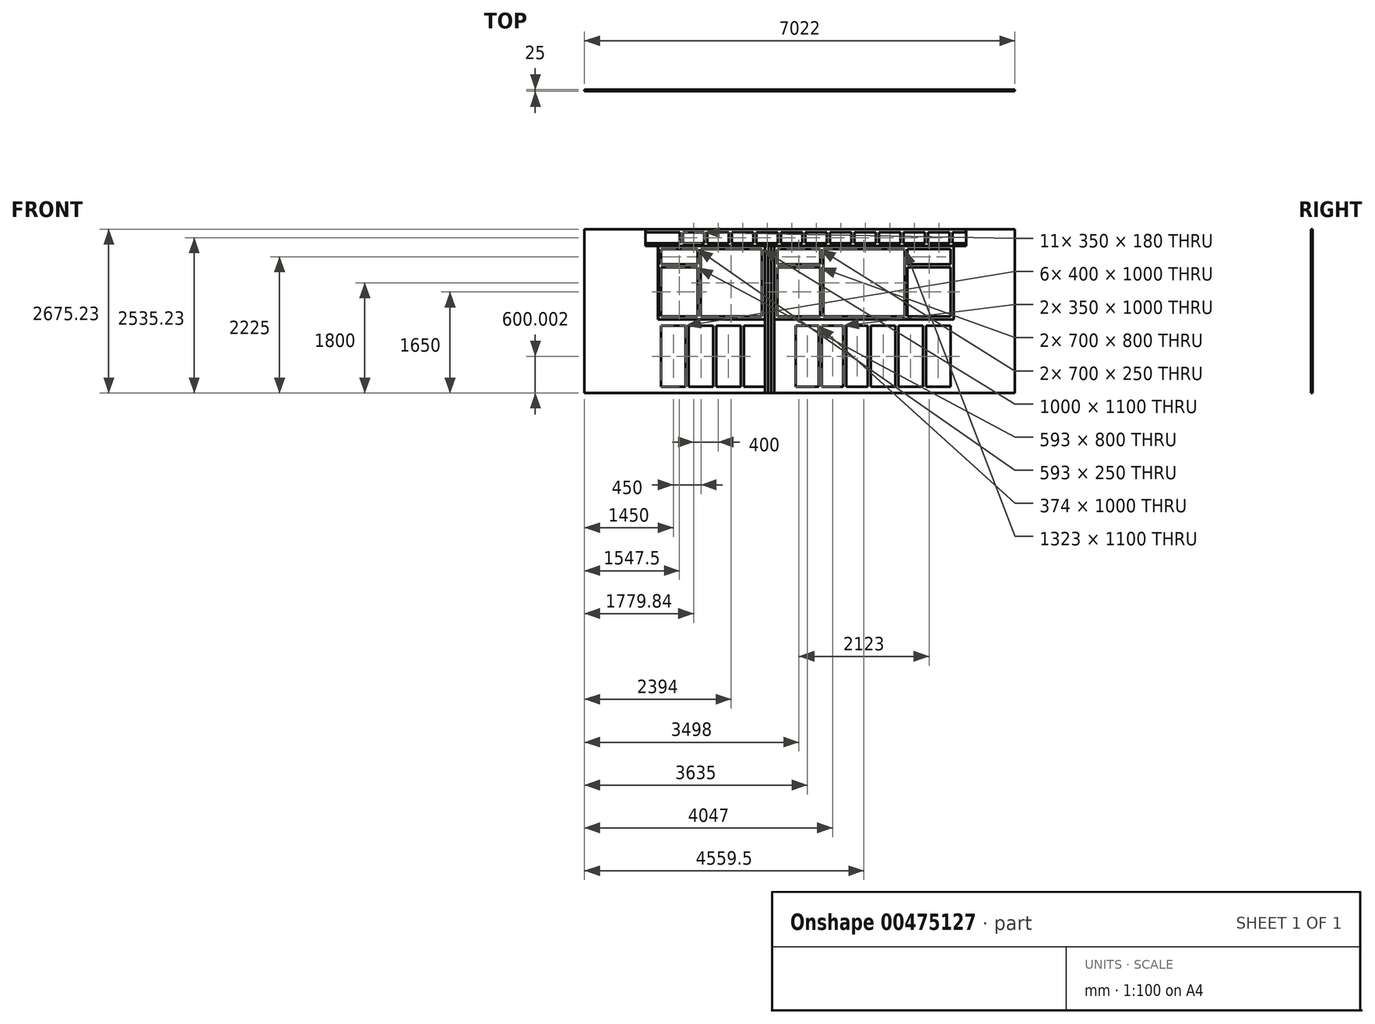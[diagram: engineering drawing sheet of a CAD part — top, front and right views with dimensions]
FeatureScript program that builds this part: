
annotation { "Feature Type Name" : "Feature", "Feature Type Description" : "" }
export const myFeature = defineFeature(function(context is Context, id is Id, definition is map)
    precondition{}
    {
        {
            var Q0;
            Q0=qCreatedBy(makeId("Front.planeOp"),FACE);
            var sketch = newSketch(context, id + "F0", { "sketchPlane" : qUnion([Q0])});
            skLineSegment(sketch, "E0.bottom", {"start": v(-708.07, 267.82) * mm, "end": v(4511.93, 267.82) * mm});
            skLineSegment(sketch, "E0.top", {"start": v(-708.07, 217.82) * mm, "end": v(4511.93, 217.82) * mm});
            skLineSegment(sketch, "E0.left", {"start": v(-708.07, 267.82) * mm, "end": v(-708.07, 217.82) * mm});
            skLineSegment(sketch, "E0.right", {"start": v(4511.93, 267.82) * mm, "end": v(4511.93, 217.82) * mm});
            skPoint(sketch, "E1.firstSnap0", {"position": v(-708.07, 242.82) * mm});
            skLineSegment(sketch, "E1.bottom", {"start": v(-708.07, 37.82) * mm, "end": v(4511.93, 37.82) * mm});
            skLineSegment(sketch, "E1.top", {"start": v(-708.07, -6.4) * mm, "end": v(4511.93, -6.4) * mm});
            skLineSegment(sketch, "E1.left", {"start": v(-708.07, 37.82) * mm, "end": v(-708.07, -6.4) * mm});
            skLineSegment(sketch, "E1.right", {"start": v(4511.93, 37.82) * mm, "end": v(4511.93, -6.4) * mm});
            skLineSegment(sketch, "E2.bottom", {"start": v(-554.23, 217.82) * mm, "end": v(-504.23, 217.82) * mm});
            skLineSegment(sketch, "E2.top", {"start": v(-554.23, 37.82) * mm, "end": v(-504.23, 37.82) * mm});
            skLineSegment(sketch, "E2.left", {"start": v(-554.23, 217.82) * mm, "end": v(-554.23, 37.82) * mm});
            skLineSegment(sketch, "E2.right", {"start": v(-504.23, 217.82) * mm, "end": v(-504.23, 37.82) * mm});
            skLineSegment(sketch, "E3.1.0.0", {"start": v(-154.23, 217.82) * mm, "end": v(-154.23, 37.82) * mm});
            skLineSegment(sketch, "E3.1.0.1", {"start": v(-104.23, 217.82) * mm, "end": v(-104.23, 37.82) * mm});
            skLineSegment(sketch, "E3.1.0.2", {"start": v(-154.23, 217.82) * mm, "end": v(-104.23, 217.82) * mm});
            skLineSegment(sketch, "E3.2.0.0", {"start": v(245.77, 217.82) * mm, "end": v(245.77, 37.82) * mm});
            skLineSegment(sketch, "E3.2.0.1", {"start": v(295.77, 217.82) * mm, "end": v(295.77, 37.82) * mm});
            skLineSegment(sketch, "E3.2.0.2", {"start": v(245.77, 217.82) * mm, "end": v(295.77, 217.82) * mm});
            skLineSegment(sketch, "E3.3.0.0", {"start": v(645.77, 217.82) * mm, "end": v(645.77, 37.82) * mm});
            skLineSegment(sketch, "E3.3.0.1", {"start": v(695.77, 217.82) * mm, "end": v(695.77, 37.82) * mm});
            skLineSegment(sketch, "E3.3.0.2", {"start": v(645.77, 217.82) * mm, "end": v(695.77, 217.82) * mm});
            skLineSegment(sketch, "E3.4.0.0", {"start": v(1045.77, 217.82) * mm, "end": v(1045.77, 37.82) * mm});
            skLineSegment(sketch, "E3.4.0.1", {"start": v(1095.77, 217.82) * mm, "end": v(1095.77, 37.82) * mm});
            skLineSegment(sketch, "E3.4.0.2", {"start": v(1045.77, 217.82) * mm, "end": v(1095.77, 217.82) * mm});
            skLineSegment(sketch, "E3.5.0.0", {"start": v(1445.77, 217.82) * mm, "end": v(1445.77, 37.82) * mm});
            skLineSegment(sketch, "E3.5.0.1", {"start": v(1495.77, 217.82) * mm, "end": v(1495.77, 37.82) * mm});
            skLineSegment(sketch, "E3.5.0.2", {"start": v(1445.77, 217.82) * mm, "end": v(1495.77, 217.82) * mm});
            skLineSegment(sketch, "E3.6.0.0", {"start": v(1845.77, 217.82) * mm, "end": v(1845.77, 37.82) * mm});
            skLineSegment(sketch, "E3.6.0.1", {"start": v(1895.77, 217.82) * mm, "end": v(1895.77, 37.82) * mm});
            skLineSegment(sketch, "E3.6.0.2", {"start": v(1845.77, 217.82) * mm, "end": v(1895.77, 217.82) * mm});
            skLineSegment(sketch, "E3.7.0.0", {"start": v(2245.77, 217.82) * mm, "end": v(2245.77, 37.82) * mm});
            skLineSegment(sketch, "E3.7.0.1", {"start": v(2295.77, 217.82) * mm, "end": v(2295.77, 37.82) * mm});
            skLineSegment(sketch, "E3.7.0.2", {"start": v(2245.77, 217.82) * mm, "end": v(2295.77, 217.82) * mm});
            skLineSegment(sketch, "E3.8.0.0", {"start": v(2645.77, 217.82) * mm, "end": v(2645.77, 37.82) * mm});
            skLineSegment(sketch, "E3.8.0.1", {"start": v(2695.77, 217.82) * mm, "end": v(2695.77, 37.82) * mm});
            skLineSegment(sketch, "E3.8.0.2", {"start": v(2645.77, 217.82) * mm, "end": v(2695.77, 217.82) * mm});
            skLineSegment(sketch, "E3.9.0.0", {"start": v(3045.77, 217.82) * mm, "end": v(3045.77, 37.82) * mm});
            skLineSegment(sketch, "E3.9.0.1", {"start": v(3095.77, 217.82) * mm, "end": v(3095.77, 37.82) * mm});
            skLineSegment(sketch, "E3.9.0.2", {"start": v(3045.77, 217.82) * mm, "end": v(3095.77, 217.82) * mm});
            skLineSegment(sketch, "E3.direction1", {"start": v(-554.23, 37.82) * mm, "end": v(-154.23, 37.82) * mm, "construction": true});
            skLineSegment(sketch, "E4.1.0.0", {"start": v(3445.77, 217.82) * mm, "end": v(3445.77, 37.82) * mm});
            skLineSegment(sketch, "E4.1.0.1", {"start": v(3495.77, 217.82) * mm, "end": v(3495.77, 37.82) * mm});
            skLineSegment(sketch, "E4.2.0.0", {"start": v(3845.77, 217.82) * mm, "end": v(3845.77, 37.82) * mm});
            skLineSegment(sketch, "E4.2.0.1", {"start": v(3895.77, 217.82) * mm, "end": v(3895.77, 37.82) * mm});
            skLineSegment(sketch, "E4.3.0.0", {"start": v(4245.77, 217.82) * mm, "end": v(4245.77, 37.82) * mm});
            skLineSegment(sketch, "E4.3.0.1", {"start": v(4295.77, 217.82) * mm, "end": v(4295.77, 37.82) * mm});
            skLineSegment(sketch, "E4.direction1", {"start": v(3045.77, 37.82) * mm, "end": v(3445.77, 37.82) * mm, "construction": true});
            skSolve(sketch);
        }
        {
            var Q0;
            Q0=makeQuery(id+"F0.imprint","IMPRINT",FACE,{"disambiguationData":[TD([[makeQuery(id+"F0.imprint","IMPRINT",EDGE,{"derivedFrom":sQuery(id+"F0.wireOp",EDGE,"E2.bottom")}),-1.0]])]});
            var Q1;
            Q1=makeQuery(id+"F0.imprint","IMPRINT",FACE,{"disambiguationData":[TD([[makeQuery(id+"F0.imprint","IMPRINT",EDGE,{"derivedFrom":sQuery(id+"F0.wireOp",EDGE,"E0.bottom")}),-1.0]])]});
            var Q2;
            Q2=makeQuery(id+"F0.imprint","IMPRINT",FACE,{"disambiguationData":[TD([[makeQuery(id+"F0.imprint","IMPRINT",EDGE,{"derivedFrom":sQuery(id+"F0.wireOp",EDGE,"E1.top")}),1.0]])]});
            var Q3;
            {var subQ0=sQuery(id+"F0.wireOp",EDGE,"E3.1.0.0");Q3=makeQuery(id+"F0.imprint","IMPRINT",FACE,{"disambiguationData":[TD([[makeQuery(id+"F0.imprint","IMPRINT",EDGE,{"derivedFrom":subQ0}),1.0]])]});}
            var Q4;
            {var subQ0=sQuery(id+"F0.wireOp",EDGE,"E3.2.0.0");Q4=makeQuery(id+"F0.imprint","IMPRINT",FACE,{"disambiguationData":[TD([[makeQuery(id+"F0.imprint","IMPRINT",EDGE,{"derivedFrom":subQ0}),1.0]])]});}
            var Q5;
            {var subQ0=sQuery(id+"F0.wireOp",EDGE,"E3.3.0.0");Q5=makeQuery(id+"F0.imprint","IMPRINT",FACE,{"disambiguationData":[TD([[makeQuery(id+"F0.imprint","IMPRINT",EDGE,{"derivedFrom":subQ0}),1.0]])]});}
            var Q6;
            {var subQ0=sQuery(id+"F0.wireOp",EDGE,"E3.4.0.0");Q6=makeQuery(id+"F0.imprint","IMPRINT",FACE,{"disambiguationData":[TD([[makeQuery(id+"F0.imprint","IMPRINT",EDGE,{"derivedFrom":subQ0}),1.0]])]});}
            var Q7;
            {var subQ0=sQuery(id+"F0.wireOp",EDGE,"E3.5.0.0");Q7=makeQuery(id+"F0.imprint","IMPRINT",FACE,{"disambiguationData":[TD([[makeQuery(id+"F0.imprint","IMPRINT",EDGE,{"derivedFrom":subQ0}),1.0]])]});}
            var Q8;
            {var subQ0=sQuery(id+"F0.wireOp",EDGE,"E3.6.0.0");Q8=makeQuery(id+"F0.imprint","IMPRINT",FACE,{"disambiguationData":[TD([[makeQuery(id+"F0.imprint","IMPRINT",EDGE,{"derivedFrom":subQ0}),1.0]])]});}
            var Q9;
            {var subQ0=sQuery(id+"F0.wireOp",EDGE,"E3.7.0.0");Q9=makeQuery(id+"F0.imprint","IMPRINT",FACE,{"disambiguationData":[TD([[makeQuery(id+"F0.imprint","IMPRINT",EDGE,{"derivedFrom":subQ0}),1.0]])]});}
            var Q10;
            {var subQ0=sQuery(id+"F0.wireOp",EDGE,"E3.8.0.0");Q10=makeQuery(id+"F0.imprint","IMPRINT",FACE,{"disambiguationData":[TD([[makeQuery(id+"F0.imprint","IMPRINT",EDGE,{"derivedFrom":subQ0}),1.0]])]});}
            var Q11;
            {var subQ0=sQuery(id+"F0.wireOp",EDGE,"E3.9.0.0");Q11=makeQuery(id+"F0.imprint","IMPRINT",FACE,{"disambiguationData":[TD([[makeQuery(id+"F0.imprint","IMPRINT",EDGE,{"derivedFrom":subQ0}),1.0]])]});}
            var Q12;
            {var subQ0=sQuery(id+"F0.wireOp",EDGE,"E4.1.0.0");Q12=makeQuery(id+"F0.imprint","IMPRINT",FACE,{"disambiguationData":[TD([[makeQuery(id+"F0.imprint","IMPRINT",EDGE,{"derivedFrom":subQ0}),1.0]])]});}
            var Q13;
            {var subQ0=sQuery(id+"F0.wireOp",EDGE,"E4.2.0.0");Q13=makeQuery(id+"F0.imprint","IMPRINT",FACE,{"disambiguationData":[TD([[makeQuery(id+"F0.imprint","IMPRINT",EDGE,{"derivedFrom":subQ0}),1.0]])]});}
            var Q14;
            {var subQ0=sQuery(id+"F0.wireOp",EDGE,"E4.3.0.0");Q14=makeQuery(id+"F0.imprint","IMPRINT",FACE,{"disambiguationData":[TD([[makeQuery(id+"F0.imprint","IMPRINT",EDGE,{"derivedFrom":subQ0}),1.0]])]});}
            extrude(context, id + "F1", {"entities" : qUnion([Q0, Q1, Q2, Q3, Q4, Q5, Q6, Q7, Q8, Q9, Q10, Q11, Q12, Q13, Q14]), "depth" : 25 * mm, "offsetDistance" : 25 * mm});
        }
        {
            var Q0;
            Q0=qCreatedBy(makeId("Front.planeOp"),FACE);
            var sketch = newSketch(context, id + "F2", { "sketchPlane" : qUnion([Q0])});
            skLineSegment(sketch, "E5.bottom", {"start": v(1235.93, -7.4) * mm, "end": v(1285.93, -7.4) * mm});
            skLineSegment(sketch, "E5.top", {"start": v(1235.93, -2407.4) * mm, "end": v(1285.93, -2407.4) * mm});
            skLineSegment(sketch, "E5.left", {"start": v(1235.93, -7.4) * mm, "end": v(1235.93, -2407.4) * mm});
            skLineSegment(sketch, "E5.right", {"start": v(1285.93, -7.4) * mm, "end": v(1285.93, -2407.4) * mm});
            skLineSegment(sketch, "E6.bottom", {"start": v(1286.93, -7.4) * mm, "end": v(1336.93, -7.4) * mm});
            skLineSegment(sketch, "E6.top", {"start": v(1286.93, -2407.4) * mm, "end": v(1336.93, -2407.4) * mm});
            skLineSegment(sketch, "E6.left", {"start": v(1286.93, -7.4) * mm, "end": v(1286.93, -2407.4) * mm});
            skLineSegment(sketch, "E6.right", {"start": v(1336.93, -7.4) * mm, "end": v(1336.93, -2407.4) * mm});
            skLineSegment(sketch, "E7.bottom", {"start": v(1337.93, -7.4) * mm, "end": v(1387.93, -7.4) * mm});
            skLineSegment(sketch, "E7.top", {"start": v(1337.93, -2407.4) * mm, "end": v(1387.93, -2407.4) * mm});
            skLineSegment(sketch, "E7.left", {"start": v(1337.93, -7.4) * mm, "end": v(1337.93, -2407.4) * mm});
            skLineSegment(sketch, "E7.right", {"start": v(1387.93, -7.4) * mm, "end": v(1387.93, -2407.4) * mm});
            skPoint(sketch, "E8", {"position": v(1311.93, -7.4) * mm});
            skSolve(sketch);
        }
        {
            var Q0;
            Q0=makeQuery(id+"F2.imprint","IMPRINT",FACE,{"disambiguationData":[TD([[makeQuery(id+"F2.imprint","IMPRINT",EDGE,{"derivedFrom":sQuery(id+"F2.wireOp",EDGE,"E5.bottom")}),-1.0]])]});
            var Q1;
            Q1=makeQuery(id+"F2.imprint","IMPRINT",FACE,{"disambiguationData":[TD([[makeQuery(id+"F2.imprint","IMPRINT",EDGE,{"derivedFrom":sQuery(id+"F2.wireOp",EDGE,"E6.bottom")}),-1.0]])]});
            var Q2;
            Q2=makeQuery(id+"F2.imprint","IMPRINT",FACE,{"disambiguationData":[TD([[makeQuery(id+"F2.imprint","IMPRINT",EDGE,{"derivedFrom":sQuery(id+"F2.wireOp",EDGE,"E7.bottom")}),-1.0]])]});
            extrude(context, id + "F3", {"entities" : qUnion([Q0, Q1, Q2]), "depth" : 25 * mm, "offsetDistance" : 25 * mm});
        }
        {
            var Q0;
            Q0=qCreatedBy(makeId("Front.planeOp"),FACE);
            var sketch = newSketch(context, id + "F4", { "sketchPlane" : qUnion([Q0])});
            skLineSegment(sketch, "E9.bottom", {"start": v(-508.07, -7.4) * mm, "end": v(1234.93, -7.4) * mm});
            skLineSegment(sketch, "E9.top", {"start": v(-508.07, -1207.4) * mm, "end": v(1234.93, -1207.4) * mm});
            skLineSegment(sketch, "E9.left", {"start": v(-508.07, -7.4) * mm, "end": v(-508.07, -1207.4) * mm});
            skLineSegment(sketch, "E9.right", {"start": v(1234.93, -7.4) * mm, "end": v(1234.93, -1207.4) * mm});
            skLineSegment(sketch, "E10.bottom", {"start": v(-458.07, -57.4) * mm, "end": v(134.93, -57.4) * mm});
            skLineSegment(sketch, "E10.top", {"start": v(-458.07, -307.4) * mm, "end": v(134.93, -307.4) * mm});
            skLineSegment(sketch, "E10.left", {"start": v(-458.07, -57.4) * mm, "end": v(-458.07, -307.4) * mm});
            skLineSegment(sketch, "E10.right", {"start": v(134.93, -57.4) * mm, "end": v(134.93, -307.4) * mm});
            skLineSegment(sketch, "E11.bottom", {"start": v(-458.07, -357.4) * mm, "end": v(134.93, -357.4) * mm});
            skLineSegment(sketch, "E11.top", {"start": v(-458.07, -1157.4) * mm, "end": v(134.93, -1157.4) * mm});
            skLineSegment(sketch, "E11.left", {"start": v(-458.07, -357.4) * mm, "end": v(-458.07, -1157.4) * mm});
            skLineSegment(sketch, "E11.right", {"start": v(134.93, -357.4) * mm, "end": v(134.93, -1157.4) * mm});
            skLineSegment(sketch, "E12.bottom", {"start": v(184.93, -57.4) * mm, "end": v(1184.93, -57.4) * mm});
            skLineSegment(sketch, "E12.top", {"start": v(184.93, -1157.4) * mm, "end": v(1184.93, -1157.4) * mm});
            skLineSegment(sketch, "E12.left", {"start": v(184.93, -57.4) * mm, "end": v(184.93, -1157.4) * mm});
            skLineSegment(sketch, "E12.right", {"start": v(1184.93, -57.4) * mm, "end": v(1184.93, -1157.4) * mm});
            skSolve(sketch);
        }
        {
            var Q0;
            Q0 = qSketchRegion(id + "F4", true);
            extrude(context, id + "F5", {"entities" : qUnion([Q0]), "depth" : 25 * mm, "offsetDistance" : 25 * mm});
        }
        {
            var Q0;
            Q0=qCreatedBy(makeId("Front.planeOp"),FACE);
            var sketch = newSketch(context, id + "F6", { "sketchPlane" : qUnion([Q0])});
            skLineSegment(sketch, "E13", {"start": v(-1709.07, -7.4) * mm, "end": v(-509.07, -7.4) * mm});
            skLineSegment(sketch, "E14", {"start": v(-509.07, -7.4) * mm, "end": v(-509.07, -1208.4) * mm});
            skLineSegment(sketch, "E15", {"start": v(-509.07, -1208.4) * mm, "end": v(1234.93, -1208.4) * mm});
            skLineSegment(sketch, "E16", {"start": v(1234.93, -1208.4) * mm, "end": v(1234.93, -2407.4) * mm});
            skLineSegment(sketch, "E17", {"start": v(1234.93, -2407.4) * mm, "end": v(-1709.07, -2407.4) * mm});
            skLineSegment(sketch, "E18", {"start": v(-1709.07, -2407.4) * mm, "end": v(-1709.07, -7.4) * mm});
            skLineSegment(sketch, "E19", {"start": v(-713.07, -7.4) * mm, "end": v(-713.07, 267.82) * mm});
            skLineSegment(sketch, "E20", {"start": v(-1709.07, -7.4) * mm, "end": v(-1709.07, 267.82) * mm});
            skLineSegment(sketch, "E21", {"start": v(-1709.07, 267.82) * mm, "end": v(-713.07, 267.82) * mm});
            skSolve(sketch);
        }
        {
            var Q0;
            Q0 = qSketchRegion(id + "F6", true);
            extrude(context, id + "F7", {"entities" : qUnion([Q0]), "depth" : 25 * mm, "offsetDistance" : 25 * mm});
        }
        {
            var Q0;
            Q0=qCreatedBy(makeId("Front.planeOp"),FACE);
            var sketch = newSketch(context, id + "F8", { "sketchPlane" : qUnion([Q0])});
            skLineSegment(sketch, "E22.bottom", {"start": v(1388.93, -7.4) * mm, "end": v(4311.93, -7.4) * mm});
            skLineSegment(sketch, "E22.top", {"start": v(1388.93, -1207.4) * mm, "end": v(4311.93, -1207.4) * mm});
            skLineSegment(sketch, "E22.left", {"start": v(1388.93, -7.4) * mm, "end": v(1388.93, -1207.4) * mm});
            skLineSegment(sketch, "E22.right", {"start": v(4311.93, -7.4) * mm, "end": v(4311.93, -1207.4) * mm});
            skLineSegment(sketch, "E23.bottom", {"start": v(1438.93, -57.4) * mm, "end": v(2138.93, -57.4) * mm});
            skLineSegment(sketch, "E23.top", {"start": v(1438.93, -307.4) * mm, "end": v(2138.93, -307.4) * mm});
            skLineSegment(sketch, "E23.left", {"start": v(1438.93, -57.4) * mm, "end": v(1438.93, -307.4) * mm});
            skLineSegment(sketch, "E23.right", {"start": v(2138.93, -57.4) * mm, "end": v(2138.93, -307.4) * mm});
            skLineSegment(sketch, "E24.bottom", {"start": v(1438.93, -357.4) * mm, "end": v(2138.93, -357.4) * mm});
            skLineSegment(sketch, "E24.top", {"start": v(1438.93, -1157.4) * mm, "end": v(2138.93, -1157.4) * mm});
            skLineSegment(sketch, "E24.left", {"start": v(1438.93, -357.4) * mm, "end": v(1438.93, -1157.4) * mm});
            skLineSegment(sketch, "E24.right", {"start": v(2138.93, -357.4) * mm, "end": v(2138.93, -1157.4) * mm});
            skLineSegment(sketch, "E25.bottom", {"start": v(2188.93, -57.4) * mm, "end": v(3511.93, -57.4) * mm});
            skLineSegment(sketch, "E25.top", {"start": v(2188.93, -1157.4) * mm, "end": v(3511.93, -1157.4) * mm});
            skLineSegment(sketch, "E25.left", {"start": v(2188.93, -57.4) * mm, "end": v(2188.93, -1157.4) * mm});
            skLineSegment(sketch, "E25.right", {"start": v(3511.93, -57.4) * mm, "end": v(3511.93, -1157.4) * mm});
            skLineSegment(sketch, "E26.bottom", {"start": v(3561.93, -57.4) * mm, "end": v(4261.93, -57.4) * mm});
            skLineSegment(sketch, "E26.top", {"start": v(3561.93, -307.4) * mm, "end": v(4261.93, -307.4) * mm});
            skLineSegment(sketch, "E26.left", {"start": v(3561.93, -57.4) * mm, "end": v(3561.93, -307.4) * mm});
            skLineSegment(sketch, "E26.right", {"start": v(4261.93, -57.4) * mm, "end": v(4261.93, -307.4) * mm});
            skLineSegment(sketch, "E27.bottom", {"start": v(3561.93, -357.4) * mm, "end": v(4261.93, -357.4) * mm});
            skLineSegment(sketch, "E27.top", {"start": v(3561.93, -1157.4) * mm, "end": v(4261.93, -1157.4) * mm});
            skLineSegment(sketch, "E27.left", {"start": v(3561.93, -357.4) * mm, "end": v(3561.93, -1157.4) * mm});
            skLineSegment(sketch, "E27.right", {"start": v(4261.93, -357.4) * mm, "end": v(4261.93, -1157.4) * mm});
            skSolve(sketch);
        }
        {
            var Q0;
            Q0 = qSketchRegion(id + "F8", true);
            extrude(context, id + "F9", {"entities" : qUnion([Q0]), "depth" : 25 * mm, "offsetDistance" : 25 * mm});
        }
        {
            var Q0;
            Q0=qCreatedBy(makeId("Front.planeOp"),FACE);
            var sketch = newSketch(context, id + "F10", { "sketchPlane" : qUnion([Q0])});
            skLineSegment(sketch, "E28", {"start": v(1388.93, -1208.4) * mm, "end": v(1388.93, -2407.4) * mm});
            skLineSegment(sketch, "E29", {"start": v(1388.93, -2407.4) * mm, "end": v(5312.93, -2407.4) * mm});
            skLineSegment(sketch, "E30", {"start": v(5312.93, -2407.4) * mm, "end": v(5312.93, 267.82) * mm});
            skLineSegment(sketch, "E31", {"start": v(5312.93, 267.82) * mm, "end": v(4516.93, 267.82) * mm});
            skLineSegment(sketch, "E32", {"start": v(4516.93, 267.82) * mm, "end": v(4516.93, -7.4) * mm});
            skLineSegment(sketch, "E33", {"start": v(4516.93, -7.4) * mm, "end": v(4312.93, -7.4) * mm});
            skLineSegment(sketch, "E34", {"start": v(4312.93, -7.4) * mm, "end": v(4312.93, -1208.4) * mm});
            skLineSegment(sketch, "E35", {"start": v(4312.93, -1208.4) * mm, "end": v(1388.93, -1208.4) * mm});
            skSolve(sketch);
        }
        {
            var Q0;
            Q0 = qSketchRegion(id + "F10", true);
            extrude(context, id + "F11", {"entities" : qUnion([Q0]), "depth" : 25 * mm, "offsetDistance" : 25 * mm});
        }
        {
            var Q0;
            Q0=makeQuery(id+"F7.opExtrude","CAP_FACE",FACE,{"disambiguationData":[OSD([sQuery(id+"F6.wireOp",EDGE,"E13"),sQuery(id+"F6.wireOp",EDGE,"E14"),sQuery(id+"F6.wireOp",EDGE,"E15"),sQuery(id+"F6.wireOp",EDGE,"E16"),sQuery(id+"F6.wireOp",EDGE,"E17"),sQuery(id+"F6.wireOp",EDGE,"E18"),sQuery(id+"F6.wireOp",EDGE,"E19"),sQuery(id+"F6.wireOp",EDGE,"E20"),sQuery(id+"F6.wireOp",EDGE,"E21")])],"isStart":false});
            var sketch = newSketch(context, id + "F12", { "sketchPlane" : qUnion([Q0])});
            skLineSegment(sketch, "E36.bottom", {"start": v(-509.07, -1257.4) * mm, "end": v(-459.07, -1257.4) * mm});
            skLineSegment(sketch, "E36.top", {"start": v(-509.07, -2357.4) * mm, "end": v(-459.07, -2357.4) * mm});
            skLineSegment(sketch, "E36.left", {"start": v(-509.07, -1257.4) * mm, "end": v(-509.07, -2357.4) * mm});
            skLineSegment(sketch, "E36.right", {"start": v(-459.07, -1257.4) * mm, "end": v(-459.07, -2357.4) * mm});
            skLineSegment(sketch, "E37.bottom", {"start": v(-59.07, -1257.4) * mm, "end": v(-9.07, -1257.4) * mm});
            skLineSegment(sketch, "E37.top", {"start": v(-59.07, -2357.4) * mm, "end": v(-9.07, -2357.4) * mm});
            skLineSegment(sketch, "E37.left", {"start": v(-9.07, -1257.4) * mm, "end": v(-9.07, -2357.4) * mm});
            skLineSegment(sketch, "E37.right", {"start": v(-59.07, -1257.4) * mm, "end": v(-59.07, -2357.4) * mm});
            skLineSegment(sketch, "E38.bottom", {"start": v(390.93, -1257.4) * mm, "end": v(440.93, -1257.4) * mm});
            skLineSegment(sketch, "E38.top", {"start": v(390.93, -2357.4) * mm, "end": v(440.93, -2357.4) * mm});
            skLineSegment(sketch, "E38.left", {"start": v(390.93, -1257.4) * mm, "end": v(390.93, -2357.4) * mm});
            skLineSegment(sketch, "E38.right", {"start": v(440.93, -1257.4) * mm, "end": v(440.93, -2357.4) * mm});
            skLineSegment(sketch, "E39.bottom", {"start": v(840.93, -1257.4) * mm, "end": v(890.93, -1257.4) * mm});
            skLineSegment(sketch, "E39.top", {"start": v(840.93, -2357.4) * mm, "end": v(890.93, -2357.4) * mm});
            skLineSegment(sketch, "E39.left", {"start": v(890.93, -1257.4) * mm, "end": v(890.93, -2357.4) * mm});
            skLineSegment(sketch, "E39.right", {"start": v(840.93, -1257.4) * mm, "end": v(840.93, -2357.4) * mm});
            skLineSegment(sketch, "E40.2.0.0", {"start": v(1738.93, -1261.55) * mm, "end": v(1738.93, -2323.37) * mm});
            skLineSegment(sketch, "E40.2.0.1", {"start": v(1688.93, -1261.55) * mm, "end": v(1688.93, -2323.37) * mm});
            skLineSegment(sketch, "E40.2.0.2", {"start": v(1688.93, -1261.55) * mm, "end": v(1738.93, -1261.55) * mm});
            skLineSegment(sketch, "E40.2.0.3", {"start": v(1688.93, -2323.37) * mm, "end": v(1738.93, -2323.37) * mm});
            skLineSegment(sketch, "E40.3.0.0", {"start": v(2162.93, -1261.55) * mm, "end": v(2162.93, -2331.84) * mm});
            skLineSegment(sketch, "E40.3.0.1", {"start": v(2112.93, -1261.55) * mm, "end": v(2112.93, -2331.84) * mm});
            skLineSegment(sketch, "E40.3.0.2", {"start": v(2112.93, -1261.55) * mm, "end": v(2162.93, -1261.55) * mm});
            skLineSegment(sketch, "E40.3.0.3", {"start": v(2112.93, -2331.84) * mm, "end": v(2162.93, -2331.84) * mm});
            skLineSegment(sketch, "E40.4.0.0", {"start": v(2562.93, -1261.55) * mm, "end": v(2562.93, -2331.84) * mm});
            skLineSegment(sketch, "E40.4.0.1", {"start": v(2512.93, -1261.55) * mm, "end": v(2512.93, -2331.84) * mm});
            skLineSegment(sketch, "E40.4.0.2", {"start": v(2512.93, -1261.55) * mm, "end": v(2562.93, -1261.55) * mm});
            skLineSegment(sketch, "E40.4.0.3", {"start": v(2512.93, -2331.84) * mm, "end": v(2562.93, -2331.84) * mm});
            skLineSegment(sketch, "E40.5.0.0", {"start": v(2912.93, -1261.55) * mm, "end": v(2912.93, -2331.84) * mm});
            skLineSegment(sketch, "E40.5.0.1", {"start": v(2962.93, -1261.55) * mm, "end": v(2962.93, -2331.84) * mm});
            skLineSegment(sketch, "E40.5.0.2", {"start": v(2912.93, -1261.55) * mm, "end": v(2962.93, -1261.55) * mm});
            skLineSegment(sketch, "E40.5.0.3", {"start": v(2912.93, -2331.84) * mm, "end": v(2962.93, -2331.84) * mm});
            skLineSegment(sketch, "E40.6.0.0", {"start": v(3362.93, -1261.55) * mm, "end": v(3362.93, -2331.84) * mm});
            skLineSegment(sketch, "E40.6.0.1", {"start": v(3412.93, -1261.55) * mm, "end": v(3412.93, -2331.84) * mm});
            skLineSegment(sketch, "E40.6.0.2", {"start": v(3362.93, -1261.55) * mm, "end": v(3412.93, -1261.55) * mm});
            skLineSegment(sketch, "E40.6.0.3", {"start": v(3362.93, -2331.84) * mm, "end": v(3412.93, -2331.84) * mm});
            skLineSegment(sketch, "E40.7.0.0", {"start": v(3812.93, -1257.4) * mm, "end": v(3812.93, -2327.7) * mm});
            skLineSegment(sketch, "E40.7.0.1", {"start": v(3862.93, -1257.4) * mm, "end": v(3862.93, -2327.7) * mm});
            skLineSegment(sketch, "E40.7.0.2", {"start": v(3812.93, -1257.4) * mm, "end": v(3862.93, -1257.4) * mm});
            skLineSegment(sketch, "E40.7.0.3", {"start": v(3812.93, -2327.7) * mm, "end": v(3862.93, -2327.7) * mm});
            skLineSegment(sketch, "E41.bottom", {"start": v(-459.07, -1257.4) * mm, "end": v(1234.93, -1257.4) * mm});
            skLineSegment(sketch, "E41.top", {"start": v(-459.07, -1307.4) * mm, "end": v(1234.93, -1307.4) * mm});
            skLineSegment(sketch, "E41.left", {"start": v(-459.07, -1257.4) * mm, "end": v(-459.07, -1307.4) * mm});
            skLineSegment(sketch, "E41.right", {"start": v(1234.93, -1257.4) * mm, "end": v(1234.93, -1307.4) * mm});
            skLineSegment(sketch, "E42.bottom", {"start": v(-509.07, -2357.4) * mm, "end": v(1234.93, -2357.4) * mm});
            skLineSegment(sketch, "E42.top", {"start": v(-509.07, -2307.4) * mm, "end": v(1234.93, -2307.4) * mm});
            skLineSegment(sketch, "E42.left", {"start": v(-509.07, -2357.4) * mm, "end": v(-509.07, -2307.4) * mm});
            skLineSegment(sketch, "E42.right", {"start": v(1234.93, -2357.4) * mm, "end": v(1234.93, -2307.4) * mm});
            skLineSegment(sketch, "E43.bottom", {"start": v(4312.93, -1257.4) * mm, "end": v(1388.93, -1257.4) * mm});
            skLineSegment(sketch, "E43.top", {"start": v(4312.93, -1307.4) * mm, "end": v(1388.93, -1307.4) * mm});
            skLineSegment(sketch, "E43.left", {"start": v(4312.93, -1257.4) * mm, "end": v(4312.93, -1307.4) * mm});
            skLineSegment(sketch, "E43.right", {"start": v(1388.93, -1257.4) * mm, "end": v(1388.93, -1307.4) * mm});
            skLineSegment(sketch, "E44.bottom", {"start": v(4312.93, -2307.4) * mm, "end": v(1388.93, -2307.4) * mm});
            skLineSegment(sketch, "E44.top", {"start": v(4312.93, -2357.4) * mm, "end": v(1388.93, -2357.4) * mm});
            skLineSegment(sketch, "E44.left", {"start": v(4312.93, -2307.4) * mm, "end": v(4312.93, -2357.4) * mm});
            skLineSegment(sketch, "E44.right", {"start": v(1388.93, -2307.4) * mm, "end": v(1388.93, -2357.4) * mm});
            skLineSegment(sketch, "E45.bottom", {"start": v(4312.93, -1257.4) * mm, "end": v(4262.93, -1257.4) * mm});
            skLineSegment(sketch, "E45.top", {"start": v(4312.93, -2357.4) * mm, "end": v(4262.93, -2357.4) * mm});
            skLineSegment(sketch, "E45.left", {"start": v(4312.93, -1257.4) * mm, "end": v(4312.93, -2357.4) * mm});
            skLineSegment(sketch, "E45.right", {"start": v(4262.93, -1257.4) * mm, "end": v(4262.93, -2357.4) * mm});
            skLineSegment(sketch, "E46.bottom", {"start": v(1388.93, -1307.4) * mm, "end": v(1688.93, -1307.4) * mm});
            skLineSegment(sketch, "E46.top", {"start": v(1388.93, -2323.37) * mm, "end": v(1688.93, -2323.37) * mm});
            skLineSegment(sketch, "E46.left", {"start": v(1388.93, -1307.4) * mm, "end": v(1388.93, -2323.37) * mm});
            skLineSegment(sketch, "E46.right", {"start": v(1688.93, -1307.4) * mm, "end": v(1688.93, -2323.37) * mm});
            skSolve(sketch);
        }
        {
            var Q0;
            {var subQ0=sQuery(id+"F12.wireOp",EDGE,"E41.top");var subQ1=sQuery(id+"F12.wireOp",EDGE,"E37.left");var subQ2=makeQuery(id+"F12.imprint","INTERSECT",VERTEX,{"derivedFrom":[subQ1,subQ0]});Q0=makeQuery(id+"F12.imprint","IMPRINT",FACE,{"disambiguationData":[TD([[makeQuery(id+"F12.imprint","IMPRINT",EDGE,{"disambiguationData":[TD([[subQ2,-1.0]])],"derivedFrom":subQ1}),1.0]])]});}
            var Q1;
            {var subQ0=sQuery(id+"F12.wireOp",EDGE,"E41.top");var subQ5=sQuery(id+"F12.wireOp",EDGE,"E37.right");var subQ6=makeQuery(id+"F12.imprint","INTERSECT",VERTEX,{"derivedFrom":[subQ5,subQ0]});Q1=makeQuery(id+"F12.imprint","IMPRINT",FACE,{"disambiguationData":[TD([[makeQuery(id+"F12.imprint","IMPRINT",EDGE,{"disambiguationData":[TD([[subQ6,-1.0]])],"derivedFrom":subQ5}),-1.0]])]});}
            var Q2;
            {var subQ0=sQuery(id+"F12.wireOp",EDGE,"E41.top");var subQ1=sQuery(id+"F12.wireOp",EDGE,"E38.right");var subQ2=makeQuery(id+"F12.imprint","INTERSECT",VERTEX,{"derivedFrom":[subQ1,subQ0]});Q2=makeQuery(id+"F12.imprint","IMPRINT",FACE,{"disambiguationData":[TD([[makeQuery(id+"F12.imprint","IMPRINT",EDGE,{"disambiguationData":[TD([[subQ2,-1.0]])],"derivedFrom":subQ1}),1.0]])]});}
            var Q3;
            {var subQ0=sQuery(id+"F12.wireOp",EDGE,"E41.top");var subQ1=sQuery(id+"F12.wireOp",EDGE,"E39.left");var subQ2=makeQuery(id+"F12.imprint","INTERSECT",VERTEX,{"derivedFrom":[subQ1,subQ0]});Q3=makeQuery(id+"F12.imprint","IMPRINT",FACE,{"disambiguationData":[TD([[makeQuery(id+"F12.imprint","IMPRINT",EDGE,{"disambiguationData":[TD([[subQ2,-1.0]])],"derivedFrom":subQ1}),1.0]])]});}
            var Q4;
            {var subQ0=sQuery(id+"F12.wireOp",EDGE,"E43.top");var subQ1=sQuery(id+"F12.wireOp",EDGE,"E40.2.0.0");var subQ2=makeQuery(id+"F12.imprint","INTERSECT",VERTEX,{"derivedFrom":[subQ1,subQ0]});Q4=makeQuery(id+"F12.imprint","IMPRINT",FACE,{"disambiguationData":[TD([[makeQuery(id+"F12.imprint","IMPRINT",EDGE,{"disambiguationData":[TD([[subQ2,-1.0]])],"derivedFrom":subQ1}),1.0]])]});}
            var Q5;
            {var subQ0=sQuery(id+"F12.wireOp",EDGE,"E43.top");var subQ1=sQuery(id+"F12.wireOp",EDGE,"E40.3.0.0");var subQ2=makeQuery(id+"F12.imprint","INTERSECT",VERTEX,{"derivedFrom":[subQ1,subQ0]});Q5=makeQuery(id+"F12.imprint","IMPRINT",FACE,{"disambiguationData":[TD([[makeQuery(id+"F12.imprint","IMPRINT",EDGE,{"disambiguationData":[TD([[subQ2,-1.0]])],"derivedFrom":subQ1}),1.0]])]});}
            var Q6;
            {var subQ0=sQuery(id+"F12.wireOp",EDGE,"E43.top");var subQ1=sQuery(id+"F12.wireOp",EDGE,"E40.4.0.0");var subQ2=makeQuery(id+"F12.imprint","INTERSECT",VERTEX,{"derivedFrom":[subQ1,subQ0]});Q6=makeQuery(id+"F12.imprint","IMPRINT",FACE,{"disambiguationData":[TD([[makeQuery(id+"F12.imprint","IMPRINT",EDGE,{"disambiguationData":[TD([[subQ2,-1.0]])],"derivedFrom":subQ1}),1.0]])]});}
            var Q7;
            {var subQ0=sQuery(id+"F12.wireOp",EDGE,"E43.top");var subQ1=sQuery(id+"F12.wireOp",EDGE,"E40.5.0.1");var subQ2=makeQuery(id+"F12.imprint","INTERSECT",VERTEX,{"derivedFrom":[subQ1,subQ0]});Q7=makeQuery(id+"F12.imprint","IMPRINT",FACE,{"disambiguationData":[TD([[makeQuery(id+"F12.imprint","IMPRINT",EDGE,{"disambiguationData":[TD([[subQ2,-1.0]])],"derivedFrom":subQ1}),1.0]])]});}
            var Q8;
            {var subQ0=sQuery(id+"F12.wireOp",EDGE,"E43.top");var subQ1=sQuery(id+"F12.wireOp",EDGE,"E40.6.0.1");var subQ2=makeQuery(id+"F12.imprint","INTERSECT",VERTEX,{"derivedFrom":[subQ1,subQ0]});Q8=makeQuery(id+"F12.imprint","IMPRINT",FACE,{"disambiguationData":[TD([[makeQuery(id+"F12.imprint","IMPRINT",EDGE,{"disambiguationData":[TD([[subQ2,-1.0]])],"derivedFrom":subQ1}),1.0]])]});}
            var Q9;
            {var subQ0=sQuery(id+"F12.wireOp",EDGE,"E43.top");var subQ1=sQuery(id+"F12.wireOp",EDGE,"E40.7.0.1");var subQ2=makeQuery(id+"F12.imprint","INTERSECT",VERTEX,{"derivedFrom":[subQ1,subQ0]});Q9=makeQuery(id+"F12.imprint","IMPRINT",FACE,{"disambiguationData":[TD([[makeQuery(id+"F12.imprint","IMPRINT",EDGE,{"disambiguationData":[TD([[subQ2,-1.0]])],"derivedFrom":subQ1}),1.0]])]});}
            var Q10;
            {var subQ5=sQuery(id+"F12.wireOp",EDGE,"E46.bottom");Q10=makeQuery(id+"F12.imprint","IMPRINT",FACE,{"disambiguationData":[TD([[makeQuery(id+"F12.imprint","IMPRINT",EDGE,{"derivedFrom":subQ5}),-1.0]])]});}
            extrude(context, id + "F13", {"entities" : qUnion([Q0, Q1, Q2, Q3, Q4, Q5, Q6, Q7, Q8, Q9, Q10]), "operationType" : NewBodyOperationType.REMOVE, "oppositeDirection" : true, "depth" : 25 * mm, "offsetDistance" : 25 * mm});
        }
    });
